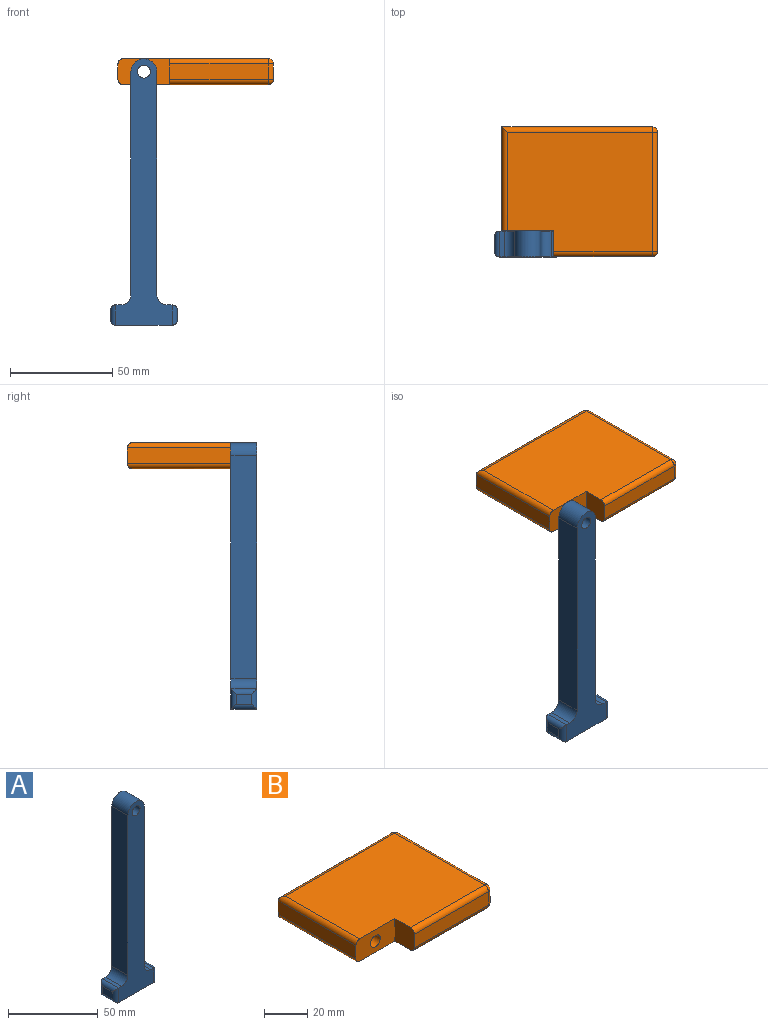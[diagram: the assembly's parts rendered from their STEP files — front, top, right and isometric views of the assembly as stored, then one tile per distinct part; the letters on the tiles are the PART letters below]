
ASSEMBLY  parts=2 mates=1
PART A: 21 faces, bbox 32.7x12.7x130.7 mm
  f0: plane 7.62x4.92mm, normal (1,0,0), area 37.5mm2, adj f13,f14,f15,f16
  f1: plane 12.7x2.39mm, normal (0,0,1), area 30.3mm2, adj f8,f9,f11,f16
  f2: plane 109.22x12.7mm, normal (1,0,0), area 1387.1mm2, adj f3,f8,f9,f11
  f3: cylinder r=6.35mm len=12.7mm, axis (0,1,0), area 253.4mm2, adj f2,f4,f8,f9
  f4: plane 109.22x12.7mm, normal (-1,0,0), area 1387.1mm2, adj f3,f8,f9,f12
  f5: plane 12.7x2.38mm, normal (0,0,1), area 30.2mm2, adj f8,f9,f12,f20
  f6: plane 7.62x4.92mm, normal (-1,0,0), area 37.5mm2, adj f17,f18,f19,f20
  f7: plane 27.63x12.7mm, normal (0,0,-1), area 350.9mm2, adj f8,f9,f13,f17
  f8: plane 130.65x27.63mm, normal (0,-1,0), area 1770.6mm2, adj f1,f2,f3,f4,f5,f7,f10,f11
  f9: plane 130.65x27.63mm, normal (0,1,0), area 1770.6mm2, adj f1,f2,f3,f4,f5,f7,f10,f11
  f10: cylinder r=3.17mm len=12.7mm, axis (0,-1,0), area 253.4mm2, adj f8,f9
  f11: cylinder r=5.08mm len=12.7mm, axis (0,-1,0), area 101.3mm2, adj f1,f2,f8,f9
  f12: cylinder r=5.08mm len=12.7mm, axis (0,1,0), area 101.3mm2, adj f4,f5,f8,f9
  f13: cylinder r=2.54mm len=12.7mm, axis (0,-1,0), area 43.3mm2, adj f0,f7,f14,f15
  f14: cylinder r=2.54mm len=10mm, axis (0,0,-1), area 32.5mm2, adj f0,f8,f13,f16
  f15: cylinder r=2.54mm len=10mm, axis (0,0,1), area 32.5mm2, adj f0,f9,f13,f16
  f16: cylinder r=2.54mm len=12.7mm, axis (0,1,0), area 43.3mm2, adj f0,f1,f14,f15
  f17: cylinder r=2.54mm len=12.7mm, axis (0,1,0), area 43.3mm2, adj f6,f7,f18,f19
  f18: cylinder r=2.54mm len=10mm, axis (0,0,1), area 32.5mm2, adj f6,f8,f17,f20
  f19: cylinder r=2.54mm len=10mm, axis (0,0,-1), area 32.5mm2, adj f6,f9,f17,f20
  f20: cylinder r=2.54mm len=12.7mm, axis (0,1,0), area 43.3mm2, adj f5,f6,f18,f19
PART B: 23 faces, bbox 76.2x63.5x12.7 mm
  f0: plane 48.26x7.62mm, normal (0,-1,0), area 367.7mm2, adj f6,f8,f13,f14
  f1: plane 71.12x58.42mm, normal (0,0,1), area 3922.6mm2, adj f6,f7,f14,f18,f20,f21
  f2: plane 50.8x7.62mm, normal (-1,0,0), area 387.1mm2, adj f5,f7,f9,f21
  f3: plane 71.12x58.42mm, normal (0,0,-1), area 3922.6mm2, adj f6,f7,f8,f9,f11,f12
  f4: plane 58.42x7.62mm, normal (1,0,0), area 445.2mm2, adj f12,f13,f17,f18
  f5: plane 73.66x7.62mm, normal (0,1,0), area 529.6mm2, adj f2,f11,f17,f20,f22
  f6: plane 12.7x12.7mm, normal (-1,0,0), area 158.5mm2, adj f0,f1,f3,f7,f8,f14
  f7: plane 25.4x12.7mm, normal (0,-1,0), area 288.1mm2, adj f1,f2,f3,f6,f9,f21,f22
  f8: cylinder r=2.54mm len=48.26mm, axis (1,0,0), area 192.5mm2, adj f0,f3,f6,f10
  f9: cylinder r=2.54mm len=50.8mm, axis (0,1,0), area 199mm2, adj f2,f3,f7,f11
  f10: sphere r=2.54mm, area 10.1mm2, adj f8,f12,f13
  f11: cylinder r=2.54mm len=73.66mm, axis (-1,0,0), area 290.2mm2, adj f3,f5,f9,f15
  f12: cylinder r=2.54mm len=58.42mm, axis (0,-1,0), area 233.1mm2, adj f3,f4,f10,f15
  f13: cylinder r=2.54mm len=7.62mm, axis (0,0,1), area 30.4mm2, adj f0,f4,f10,f16
  f14: cylinder r=2.54mm len=48.26mm, axis (-1,0,0), area 192.5mm2, adj f0,f1,f6,f16
  f15: sphere r=2.54mm, area 10.1mm2, adj f11,f12,f17
  f16: sphere r=2.54mm, area 10.1mm2, adj f13,f14,f18
  f17: cylinder r=2.54mm len=7.62mm, axis (0,0,-1), area 30.4mm2, adj f4,f5,f15,f19
  f18: cylinder r=2.54mm len=58.42mm, axis (0,1,0), area 233.1mm2, adj f1,f4,f16,f19
  f19: sphere r=2.54mm, area 10.1mm2, adj f17,f18,f20
  f20: cylinder r=2.54mm len=73.66mm, axis (1,0,0), area 290.2mm2, adj f1,f5,f19,f21
  f21: cylinder r=2.54mm len=50.8mm, axis (0,-1,0), area 199mm2, adj f1,f2,f7,f20
  f22: cylinder r=3.17mm len=50.8mm, axis (0,-1,0), area 1013.4mm2, adj f5,f7
PLACE A t=(-52.11,-10.86,53.68)mm
PLACE B t=(-64.81,-23.56,47.33)mm
MATE pin_slot B.f22 <-> A.f3  axis (0,-1,0) through (-52.11,-10.86,53.68)mm
